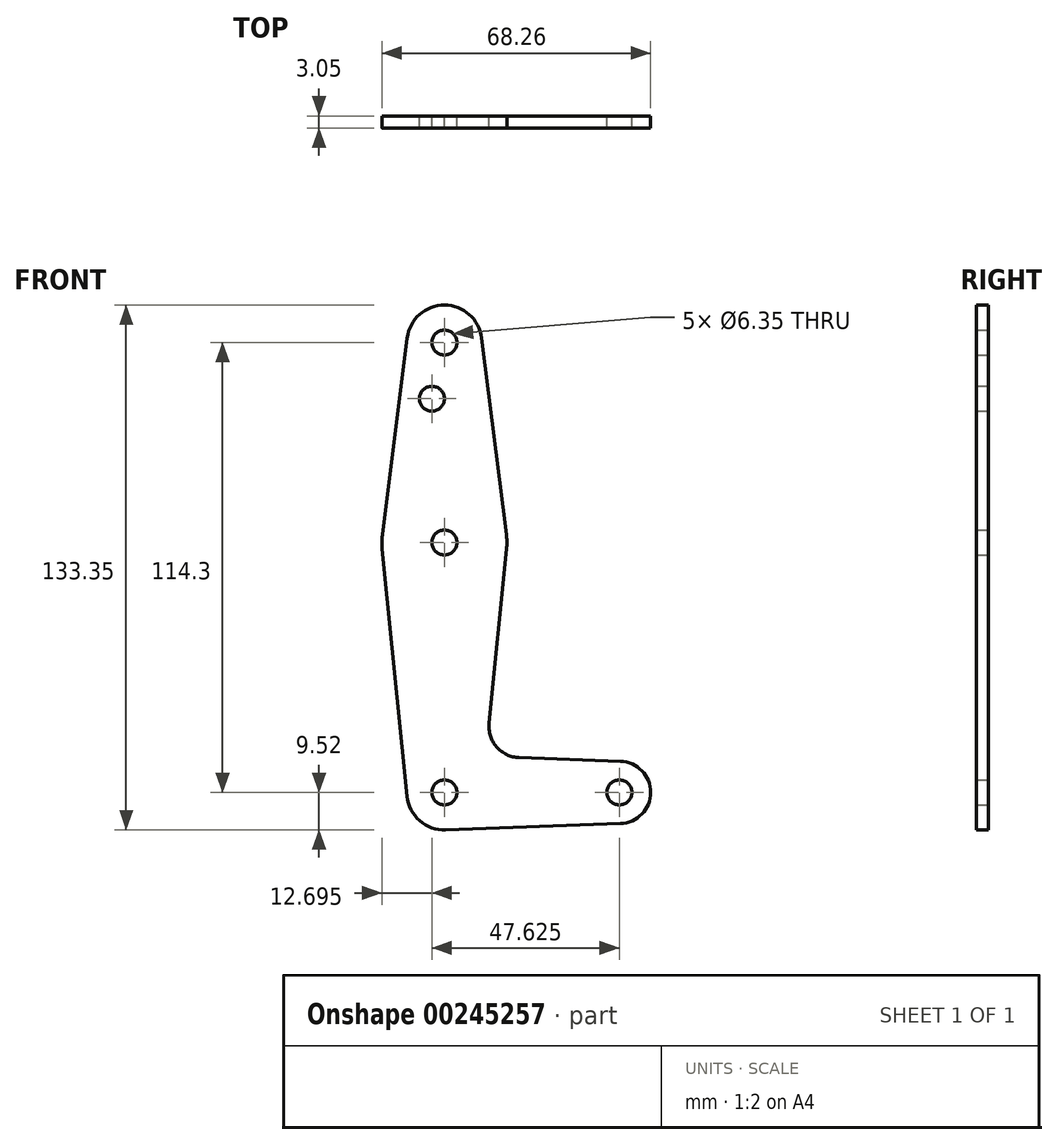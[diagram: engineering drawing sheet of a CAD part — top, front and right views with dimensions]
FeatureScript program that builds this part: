
annotation { "Feature Type Name" : "Feature", "Feature Type Description" : "" }
export const myFeature = defineFeature(function(context is Context, id is Id, definition is map)
    precondition{}
    {
        {
            var Q0;
            Q0=qCreatedBy(makeId("Front.planeOp"),FACE);
            var sketch = newSketch(context, id + "F0", { "sketchPlane" : qUnion([Q0])});
            skLineSegment(sketch, "E0", {"start": v(0, 0) * mm, "end": v(0, 114.3) * mm, "construction": true});
            skLineSegment(sketch, "E1", {"start": v(0, 0) * mm, "end": v(44.45, 0) * mm, "construction": true});
            skCircle(sketch, "E2", {"center": v(0, 0) * mm, "radius": 9.53 * mm});
            skCircle(sketch, "E3", {"center": v(0, 114.3) * mm, "radius": 9.53 * mm});
            skCircle(sketch, "E4", {"center": v(0, 63.5) * mm, "radius": 15.88 * mm});
            skCircle(sketch, "E5", {"center": v(44.45, 0) * mm, "radius": 7.94 * mm});
            skLineSegment(sketch, "E6", {"start": v(-9.45, 115.5) * mm, "end": v(-15.75, 65.48) * mm});
            skLineSegment(sketch, "E7", {"start": v(9.45, 115.5) * mm, "end": v(15.75, 65.48) * mm});
            skLineSegment(sketch, "E8", {"start": v(-9.48, -0.95) * mm, "end": v(-15.8, 61.91) * mm});
            skLineSegment(sketch, "E9", {"start": v(11.34, 17.6) * mm, "end": v(15.8, 61.91) * mm});
            skLineSegment(sketch, "E10", {"start": v(18.97, 8.85) * mm, "end": v(44.73, 7.93) * mm});
            skLineSegment(sketch, "E11", {"start": v(0.34, -9.52) * mm, "end": v(44.73, -7.93) * mm});
            skCircle(sketch, "E12", {"center": v(0, 114.3) * mm, "radius": 3.18 * mm});
            skCircle(sketch, "E13", {"center": v(-3.18, 100.03) * mm, "radius": 3.18 * mm});
            skCircle(sketch, "E14", {"center": v(0, 63.5) * mm, "radius": 3.18 * mm});
            skCircle(sketch, "E15", {"center": v(0, 0) * mm, "radius": 3.18 * mm});
            skCircle(sketch, "E16", {"center": v(44.45, 0) * mm, "radius": 3.18 * mm});
            skArc(sketch, "E17.filletArc", {"start": v(11.34, 17.6) * mm, "mid": v(13.26, 11.57) * mm, "end": v(18.97, 8.85) * mm});
            skSolve(sketch);
        }
        {
            var Q0;
            Q0 = qSketchRegion(id + "F0", true);
            extrude(context, id + "F1", {"entities" : qUnion([Q0]), "depth" : 3.05 * mm});
        }
    });
